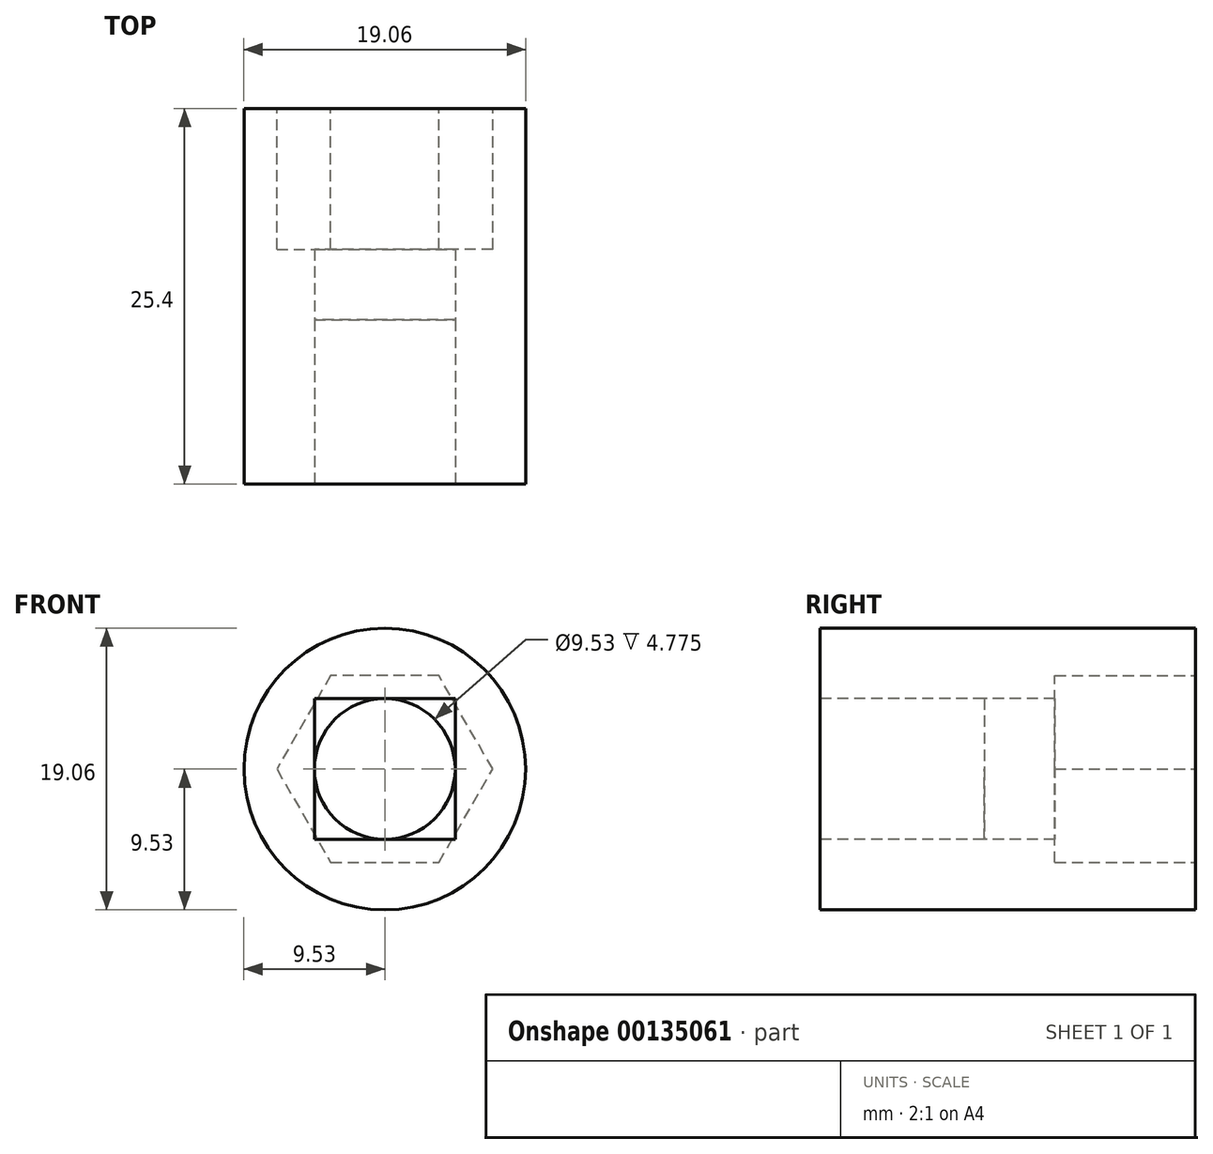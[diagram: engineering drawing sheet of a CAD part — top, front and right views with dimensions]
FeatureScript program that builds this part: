
annotation { "Feature Type Name" : "Feature", "Feature Type Description" : "" }
export const myFeature = defineFeature(function(context is Context, id is Id, definition is map)
    precondition{}
    {
        {
            var Q0;
            Q0=qCreatedBy(makeId("Front.planeOp"),FACE);
            var sketch = newSketch(context, id + "F0", { "sketchPlane" : qUnion([Q0])});
            skCircle(sketch, "E0", {"center": v(0, 0) * mm, "radius": 9.53 * mm});
            skSolve(sketch);
        }
        {
            var Q0;
            Q0 = qSketchRegion(id + "F0", true);
            extrude(context, id + "F1", {"entities" : qUnion([Q0]), "depth" : 25.4 * mm});
        }
        {
            var Q0;
            Q0=makeQuery(id+"F1.opExtrude","CAP_FACE",FACE,{"disambiguationData":[OSD([sQuery(id+"F0.wireOp",EDGE,"E0")])],"isStart":false});
            var sketch = newSketch(context, id + "F2", { "sketchPlane" : qUnion([Q0])});
            skLineSegment(sketch, "E1.bottom", {"start": v(-4.76, 4.76) * mm, "end": v(4.76, 4.76) * mm});
            skLineSegment(sketch, "E1.top", {"start": v(-4.76, -4.76) * mm, "end": v(4.76, -4.76) * mm});
            skLineSegment(sketch, "E1.left", {"start": v(-4.76, 4.76) * mm, "end": v(-4.76, -4.76) * mm});
            skLineSegment(sketch, "E1.right", {"start": v(4.76, 4.76) * mm, "end": v(4.76, -4.76) * mm});
            skPoint(sketch, "E1.middle", {"position": v(0, 0) * mm});
            skCircle(sketch, "E2", {"center": v(0, 0) * mm, "radius": 4.76 * mm});
            skSolve(sketch);
        }
        {
            var Q0;
            {var subQ0=sQuery(id+"F2.wireOp",EDGE,"E2");var subQ1=makeQuery(id+"F2.imprint","INTERSECT",VERTEX,{"derivedFrom":[sQuery(id+"F2.wireOp",EDGE,"E1.bottom"),subQ0]});Q0=makeQuery(id+"F2.imprint","IMPRINT",FACE,{"disambiguationData":[TD([[makeQuery(id+"F2.imprint","IMPRINT",EDGE,{"disambiguationData":[TD([[subQ1,1.0]])],"derivedFrom":subQ0}),1.0]])]});}
            extrude(context, id + "F3", {"entities" : qUnion([Q0]), "operationType" : NewBodyOperationType.REMOVE, "endBound" : BoundingType.THROUGH_ALL, "oppositeDirection" : true, "depth" : 25.4 * mm});
        }
        {
            var Q0;
            Q0 = qSketchRegion(id + "F2", true);
            extrude(context, id + "F4", {"entities" : qUnion([Q0]), "operationType" : NewBodyOperationType.REMOVE, "oppositeDirection" : true, "depth" : 11.1 * mm});
        }
        {
            var Q0;
            Q0=makeQuery(id+"F1.opExtrude","CAP_FACE",FACE,{"disambiguationData":[OSD([sQuery(id+"F0.wireOp",EDGE,"E0")])],"isStart":true});
            var sketch = newSketch(context, id + "F5", { "sketchPlane" : qUnion([Q0])});
            skCircle(sketch, "E3.cCircle", {"center": v(0, 0) * mm, "radius": 6.32 * mm, "construction": true});
            skLineSegment(sketch, "E3.0", {"start": v(-3.65, 6.32) * mm, "end": v(3.65, 6.32) * mm});
            skLineSegment(sketch, "E3.1", {"start": v(3.65, 6.32) * mm, "end": v(7.3, 0) * mm});
            skLineSegment(sketch, "E3.2", {"start": v(7.3, 0) * mm, "end": v(3.65, -6.32) * mm});
            skLineSegment(sketch, "E3.3", {"start": v(3.65, -6.32) * mm, "end": v(-3.65, -6.32) * mm});
            skLineSegment(sketch, "E3.4", {"start": v(-3.65, -6.32) * mm, "end": v(-7.3, 0) * mm});
            skLineSegment(sketch, "E3.5", {"start": v(-7.3, 0) * mm, "end": v(-3.65, 6.32) * mm});
            skPoint(sketch, "E3.0.midPoint", {"position": v(0, 6.32) * mm});
            skSolve(sketch);
        }
        {
            var Q0;
            Q0 = qSketchRegion(id + "F5", true);
            extrude(context, id + "F6", {"entities" : qUnion([Q0]), "operationType" : NewBodyOperationType.REMOVE, "oppositeDirection" : true, "depth" : 9.52 * mm});
        }
    });
